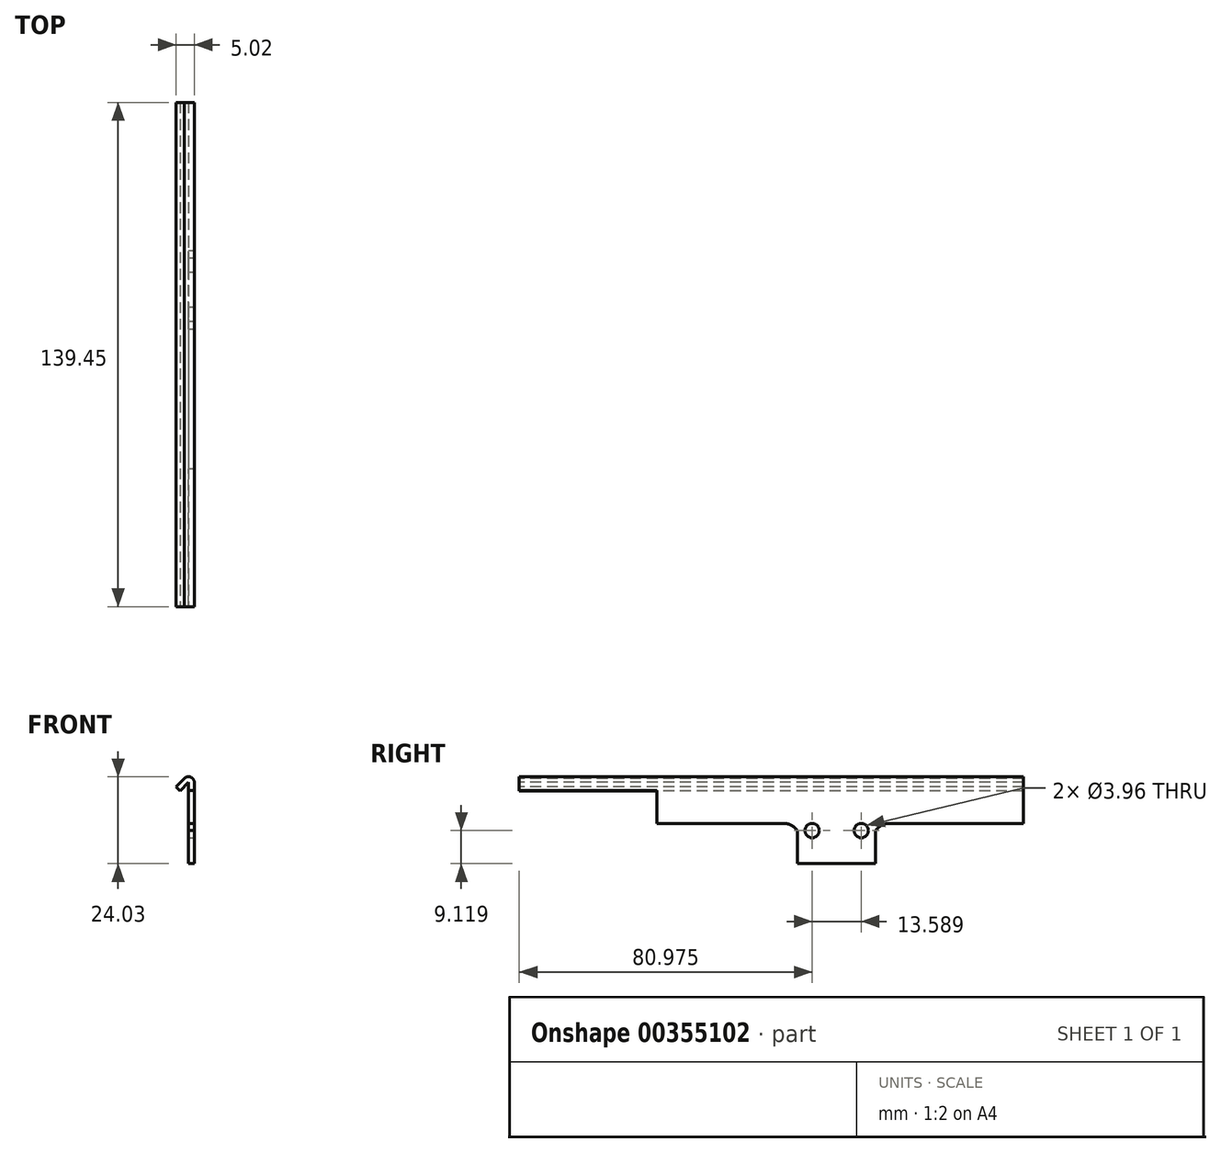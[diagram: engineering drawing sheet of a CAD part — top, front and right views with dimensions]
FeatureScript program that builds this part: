
annotation { "Feature Type Name" : "Feature", "Feature Type Description" : "" }
export const myFeature = defineFeature(function(context is Context, id is Id, definition is map)
    precondition{}
    {
        {
            var Q0;
            Q0=qCreatedBy(makeId("Right.planeOp"),FACE);
            var sketch = newSketch(context, id + "F0", { "sketchPlane" : qUnion([Q0])});
            skLineSegment(sketch, "E0.bottom", {"start": v(0, 0) * mm, "end": v(139.45, 0) * mm});
            skLineSegment(sketch, "E0.top", {"start": v(0, 24.03) * mm, "end": v(139.45, 24.03) * mm});
            skLineSegment(sketch, "E0.left", {"start": v(0, 0) * mm, "end": v(0, 24.03) * mm});
            skLineSegment(sketch, "E0.right", {"start": v(139.45, 0) * mm, "end": v(139.45, 24.03) * mm});
            skSolve(sketch);
        }
        {
            var Q0;
            Q0 = qSketchRegion(id + "F0", true);
            extrude(context, id + "F1", {"entities" : qUnion([Q0]), "depth" : 1.57 * mm});
        }
        {
            var Q0;
            Q0=makeQuery(id+"F1.opExtrude","CAP_FACE",FACE,{"disambiguationData":[OSD([sQuery(id+"F0.wireOp",EDGE,"E0.bottom"),sQuery(id+"F0.wireOp",EDGE,"E0.top"),sQuery(id+"F0.wireOp",EDGE,"E0.left"),sQuery(id+"F0.wireOp",EDGE,"E0.right")])],"isStart":false});
            var sketch = newSketch(context, id + "F2", { "sketchPlane" : qUnion([Q0])});
            skCircle(sketch, "E1", {"center": v(7.95, 14.68) * mm, "radius": 2.53 * mm});
            skCircle(sketch, "E2", {"center": v(80.98, 9.12) * mm, "radius": 1.98 * mm});
            skCircle(sketch, "E3", {"center": v(94.56, 9.12) * mm, "radius": 1.98 * mm});
            skSolve(sketch);
        }
        {
            var Q0;
            Q0 = qSketchRegion(id + "F2", true);
            extrude(context, id + "F3", {"entities" : qUnion([Q0]), "operationType" : NewBodyOperationType.REMOVE, "oppositeDirection" : true, "depth" : 25.4 * mm});
        }
        {
            var Q0;
            Q0=makeQuery(id+"F1.opExtrude","CAP_FACE",FACE,{"disambiguationData":[OSD([sQuery(id+"F0.wireOp",EDGE,"E0.bottom"),sQuery(id+"F0.wireOp",EDGE,"E0.top"),sQuery(id+"F0.wireOp",EDGE,"E0.left"),sQuery(id+"F0.wireOp",EDGE,"E0.right")])],"isStart":false});
            var sketch = newSketch(context, id + "F4", { "sketchPlane" : qUnion([Q0])});
            skLineSegment(sketch, "E4.bottom", {"start": v(0, 0) * mm, "end": v(76.86, 0) * mm});
            skLineSegment(sketch, "E4.top", {"start": v(0, 9.12) * mm, "end": v(76.86, 9.12) * mm});
            skLineSegment(sketch, "E4.left", {"start": v(0, 0) * mm, "end": v(0, 9.12) * mm});
            skLineSegment(sketch, "E4.right", {"start": v(76.86, 0) * mm, "end": v(76.86, 9.12) * mm});
            skLineSegment(sketch, "E5.bottom", {"start": v(98.55, 9.12) * mm, "end": v(139.45, 9.12) * mm});
            skLineSegment(sketch, "E5.top", {"start": v(98.55, 0) * mm, "end": v(139.45, 0) * mm});
            skLineSegment(sketch, "E5.left", {"start": v(98.55, 9.12) * mm, "end": v(98.55, 0) * mm});
            skLineSegment(sketch, "E5.right", {"start": v(139.45, 9.12) * mm, "end": v(139.45, 0) * mm});
            skSolve(sketch);
        }
        {
            var Q0;
            Q0 = qSketchRegion(id + "F4", true);
            extrude(context, id + "F5", {"entities" : qUnion([Q0]), "operationType" : NewBodyOperationType.REMOVE, "oppositeDirection" : true, "depth" : 25.4 * mm});
        }
        {
            var Q0;
            Q0=makeQuery(id+"F1.opExtrude","CAP_FACE",FACE,{"disambiguationData":[OSD([sQuery(id+"F0.wireOp",EDGE,"E0.bottom"),sQuery(id+"F0.wireOp",EDGE,"E0.top"),sQuery(id+"F0.wireOp",EDGE,"E0.left"),sQuery(id+"F0.wireOp",EDGE,"E0.right")])],"isStart":false});
            var sketch = newSketch(context, id + "F6", { "sketchPlane" : qUnion([Q0])});
            skCircle(sketch, "E6", {"center": v(102.3, 6.55) * mm, "radius": 4.55 * mm});
            skCircle(sketch, "E7", {"center": v(73.1, 6.55) * mm, "radius": 4.55 * mm});
            skCircle(sketch, "E8", {"center": v(21.31, 6.55) * mm, "radius": 4.55 * mm});
            skLineSegment(sketch, "E9", {"start": v(139.45, 11.1) * mm, "end": v(-6.02, 11.1) * mm});
            skLineSegment(sketch, "E10", {"start": v(16.76, 18.3) * mm, "end": v(16.76, -4.59) * mm});
            skSolve(sketch);
        }
        {
            var Q0;
            {var subQ0=sQuery(id+"F6.wireOp",EDGE,"E9");var subQ1=sQuery(id+"F6.wireOp",EDGE,"E6");var subQ2=makeQuery(id+"F6.imprint","INTERSECT",VERTEX,{"derivedFrom":[subQ1,subQ0]});Q0=makeQuery(id+"F6.imprint","IMPRINT",FACE,{"disambiguationData":[TD([[makeQuery(id+"F6.imprint","IMPRINT",EDGE,{"disambiguationData":[TD([[subQ2,1.0]])],"derivedFrom":subQ1}),-1.0]])]});}
            var Q1;
            {var subQ0=sQuery(id+"F6.wireOp",EDGE,"E6");var subQ1=makeQuery(id+"F6.imprint","INTERSECT",VERTEX,{"derivedFrom":[subQ0,sQuery(id+"F6.wireOp",EDGE,"E9")]});Q1=makeQuery(id+"F6.imprint","IMPRINT",FACE,{"disambiguationData":[TD([[makeQuery(id+"F6.imprint","IMPRINT",EDGE,{"disambiguationData":[TD([[subQ1,1.0]])],"derivedFrom":subQ0}),1.0]])]});}
            var Q2;
            {var subQ0=sQuery(id+"F6.wireOp",EDGE,"E8");var subQ1=makeQuery(id+"F6.imprint","INTERSECT",VERTEX,{"derivedFrom":[subQ0,sQuery(id+"F6.wireOp",EDGE,"E9")]});Q2=makeQuery(id+"F6.imprint","IMPRINT",FACE,{"disambiguationData":[TD([[makeQuery(id+"F6.imprint","IMPRINT",EDGE,{"disambiguationData":[TD([[subQ1,1.0]])],"derivedFrom":subQ0}),1.0]])]});}
            var Q3;
            {var subQ0=sQuery(id+"F6.wireOp",EDGE,"E9");var subQ1=sQuery(id+"F6.wireOp",EDGE,"E7");var subQ2=makeQuery(id+"F6.imprint","INTERSECT",VERTEX,{"derivedFrom":[subQ1,subQ0]});Q3=makeQuery(id+"F6.imprint","IMPRINT",FACE,{"disambiguationData":[TD([[makeQuery(id+"F6.imprint","IMPRINT",EDGE,{"disambiguationData":[TD([[subQ2,-1.0]])],"derivedFrom":subQ1}),-1.0]])]});}
            var Q4;
            {var subQ0=sQuery(id+"F6.wireOp",EDGE,"E7");var subQ3=makeQuery(id+"F6.imprint","INTERSECT",VERTEX,{"derivedFrom":[subQ0,sQuery(id+"F6.wireOp",EDGE,"E9")]});Q4=makeQuery(id+"F6.imprint","IMPRINT",FACE,{"disambiguationData":[TD([[makeQuery(id+"F6.imprint","IMPRINT",EDGE,{"disambiguationData":[TD([[subQ3,-1.0]])],"derivedFrom":subQ0}),1.0]])]});}
            extrude(context, id + "F7", {"entities" : qUnion([Q0, Q1, Q2, Q3, Q4]), "operationType" : NewBodyOperationType.REMOVE, "oppositeDirection" : true, "depth" : 25.4 * mm});
        }
        {
            var Q0;
            Q0=makeQuery(id+"F1.opExtrude","SWEPT_FACE",FACE,{"disambiguationData":[OSD([sQuery(id+"F0.wireOp",EDGE,"E0.left")])]});
            var sketch = newSketch(context, id + "F8", { "sketchPlane" : qUnion([Q0])});
            skLineSegment(sketch, "E11", {"start": v(-2.34, 20.11) * mm, "end": v(0, 22.45) * mm});
            skLineSegment(sketch, "E12", {"start": v(-3.45, 21.23) * mm, "end": v(-1.23, 23.45) * mm});
            skLineSegment(sketch, "E13", {"start": v(-3.45, 21.23) * mm, "end": v(-2.34, 20.11) * mm});
            skArc(sketch, "E14", {"start": v(-1.23, 23.45) * mm, "mid": v(0.53, 23.94) * mm, "end": v(1.57, 22.45) * mm});
            skLineSegment(sketch, "E15", {"start": v(-1.23, 23.45) * mm, "end": v(0, 22.45) * mm});
            skLineSegment(sketch, "E16", {"start": v(1.57, 22.45) * mm, "end": v(0, 22.45) * mm});
            skSolve(sketch);
        }
        {
            var Q0;
            {var subQ1=sQuery(id+"F0.wireOp",EDGE,"E0.left");var subQ2=makeQuery(id+"F1.opExtrude","SWEPT_EDGE",EDGE,{"disambiguationData":[OSD([sQuery(id+"F0.wireOp",EDGE,"E0.top"),subQ1])]});Q0=makeQuery(id+"F8.imprint","IMPRINT",FACE,{"disambiguationData":[TD([[makeQuery(id+"F8.imprint","IMPRINT",EDGE,{"derivedFrom":subQ2}),1.0]])]});}
            extrude(context, id + "F9", {"entities" : qUnion([Q0]), "operationType" : NewBodyOperationType.REMOVE, "endBound" : BoundingType.THROUGH_ALL, "oppositeDirection" : true, "depth" : 25.4 * mm});
        }
        {
            var Q0;
            {var subQ1=sQuery(id+"F0.wireOp",EDGE,"E0.left");var subQ2=makeQuery(id+"F1.opExtrude","CAP_EDGE",EDGE,{"disambiguationData":[OSD([subQ1])],"isStart":true});var subQ7=makeQuery(id+"F8.imprint","INTERSECT",VERTEX,{"derivedFrom":[subQ2,sQuery(id+"F8.wireOp",EDGE,"E11")]});Q0=makeQuery(id+"F8.imprint","IMPRINT",FACE,{"disambiguationData":[TD([[makeQuery(id+"F8.imprint","IMPRINT",EDGE,{"disambiguationData":[TD([[subQ7,1.0]])],"derivedFrom":subQ2}),-1.0]])]});}
            var Q1;
            {var subQ4=sQuery(id+"F8.wireOp",EDGE,"E15");Q1=makeQuery(id+"F8.imprint","IMPRINT",FACE,{"disambiguationData":[TD([[makeQuery(id+"F8.imprint","IMPRINT",EDGE,{"derivedFrom":subQ4}),1.0]])]});}
            var Q2;
            Q2=makeQuery(id+"F8.imprint","IMPRINT",FACE,{"disambiguationData":[TD([[makeQuery(id+"F8.imprint","IMPRINT",EDGE,{"derivedFrom":sQuery(id+"F8.wireOp",EDGE,"E12")}),-1.0]])]});
            extrude(context, id + "F10", {"entities" : qUnion([Q0, Q1, Q2]), "operationType" : NewBodyOperationType.ADD, "oppositeDirection" : true, "depth" : 139.45 * mm});
        }
        {
            var Q0;
            Q0=makeQuery(id+"F1.opExtrude","CAP_FACE",FACE,{"disambiguationData":[OSD([sQuery(id+"F0.wireOp",EDGE,"E0.bottom"),sQuery(id+"F0.wireOp",EDGE,"E0.top"),sQuery(id+"F0.wireOp",EDGE,"E0.left"),sQuery(id+"F0.wireOp",EDGE,"E0.right")])],"isStart":true});
            var sketch = newSketch(context, id + "F11", { "sketchPlane" : qUnion([Q0])});
            skLineSegment(sketch, "E17.bottom", {"start": v(0, 9.12) * mm, "end": v(-38.1, 9.12) * mm});
            skLineSegment(sketch, "E17.top", {"start": v(0, 20.23) * mm, "end": v(-38.1, 20.23) * mm});
            skLineSegment(sketch, "E17.left", {"start": v(0, 9.12) * mm, "end": v(0, 20.23) * mm});
            skLineSegment(sketch, "E17.right", {"start": v(-38.1, 9.12) * mm, "end": v(-38.1, 20.23) * mm});
            skSolve(sketch);
        }
        {
            var Q0;
            {var subQ5=sQuery(id+"F11.wireOp",EDGE,"E17.top");Q0=makeQuery(id+"F11.imprint","IMPRINT",FACE,{"disambiguationData":[TD([[makeQuery(id+"F11.imprint","IMPRINT",EDGE,{"derivedFrom":subQ5}),1.0]])]});}
            extrude(context, id + "F12", {"entities" : qUnion([Q0]), "operationType" : NewBodyOperationType.REMOVE, "oppositeDirection" : true, "depth" : 25.4 * mm});
        }
        {
            var Q0;
            Q0=qCreatedBy(makeId("Right.planeOp"),FACE);
            var sketch = newSketch(context, id + "F13", { "sketchPlane" : qUnion([Q0])});
            skLineSegment(sketch, "E18", {"start": v(0, 20.23) * mm, "end": v(0, 0) * mm});
            skLineSegment(sketch, "E19", {"start": v(0, 0) * mm, "end": v(16.76, 0) * mm});
            skLineSegment(sketch, "E20", {"start": v(16.76, 0) * mm, "end": v(16.76, 6.55) * mm});
            skLineSegment(sketch, "E21", {"start": v(0, 20.23) * mm, "end": v(38.1, 20.23) * mm});
            skLineSegment(sketch, "E22", {"start": v(38.1, 20.23) * mm, "end": v(38.1, 11.1) * mm});
            skLineSegment(sketch, "E23", {"start": v(38.1, 11.1) * mm, "end": v(21.31, 11.1) * mm});
            skArc(sketch, "E24", {"start": v(21.31, 11.1) * mm, "mid": v(18.1, 9.77) * mm, "end": v(16.76, 6.55) * mm});
            skSolve(sketch);
        }
        {
            var Q0;
            Q0=makeQuery(id+"F13.imprint","IMPRINT",FACE,{"disambiguationData":[TD([[makeQuery(id+"F13.imprint","IMPRINT",EDGE,{"derivedFrom":sQuery(id+"F13.wireOp",EDGE,"E18")}),1.0]])]});
            var Q1;
            Q1=makeQuery(id+"F1.opExtrude","CAP_FACE",FACE,{"disambiguationData":[OSD([sQuery(id+"F0.wireOp",EDGE,"E0.bottom"),sQuery(id+"F0.wireOp",EDGE,"E0.top"),sQuery(id+"F0.wireOp",EDGE,"E0.left"),sQuery(id+"F0.wireOp",EDGE,"E0.right")])],"isStart":false});
            extrude(context, id + "F14", {"entities" : qUnion([Q0]), "endBound" : BoundingType.UP_TO_SURFACE, "endBoundEntityFace" : qUnion([Q1]), "depth" : 25.4 * mm});
        }
        {
            var Q0;
            Q0=makeQuery(id+"F2.imprint","IMPRINT",FACE,{"disambiguationData":[TD([[makeQuery(id+"F2.imprint","IMPRINT",EDGE,{"derivedFrom":sQuery(id+"F2.wireOp",EDGE,"E1")}),1.0]])]});
            extrude(context, id + "F15", {"entities" : qUnion([Q0]), "operationType" : NewBodyOperationType.REMOVE, "oppositeDirection" : true, "depth" : 25.4 * mm});
        }
        {
            var Q0;
            Q0=makeQuery(id+"F14.opExtrude","SWEPT_BODY",BODY,{"disambiguationData":[OSD([sQuery(id+"F13.wireOp",EDGE,"E18"),sQuery(id+"F13.wireOp",EDGE,"E19"),sQuery(id+"F13.wireOp",EDGE,"E20"),sQuery(id+"F13.wireOp",EDGE,"E21"),sQuery(id+"F13.wireOp",EDGE,"E22"),sQuery(id+"F13.wireOp",EDGE,"E23"),sQuery(id+"F13.wireOp",EDGE,"E24")])]});
            deleteBodies(context, id + "F16", {"entities" : qUnion([Q0])});
        }
    });
